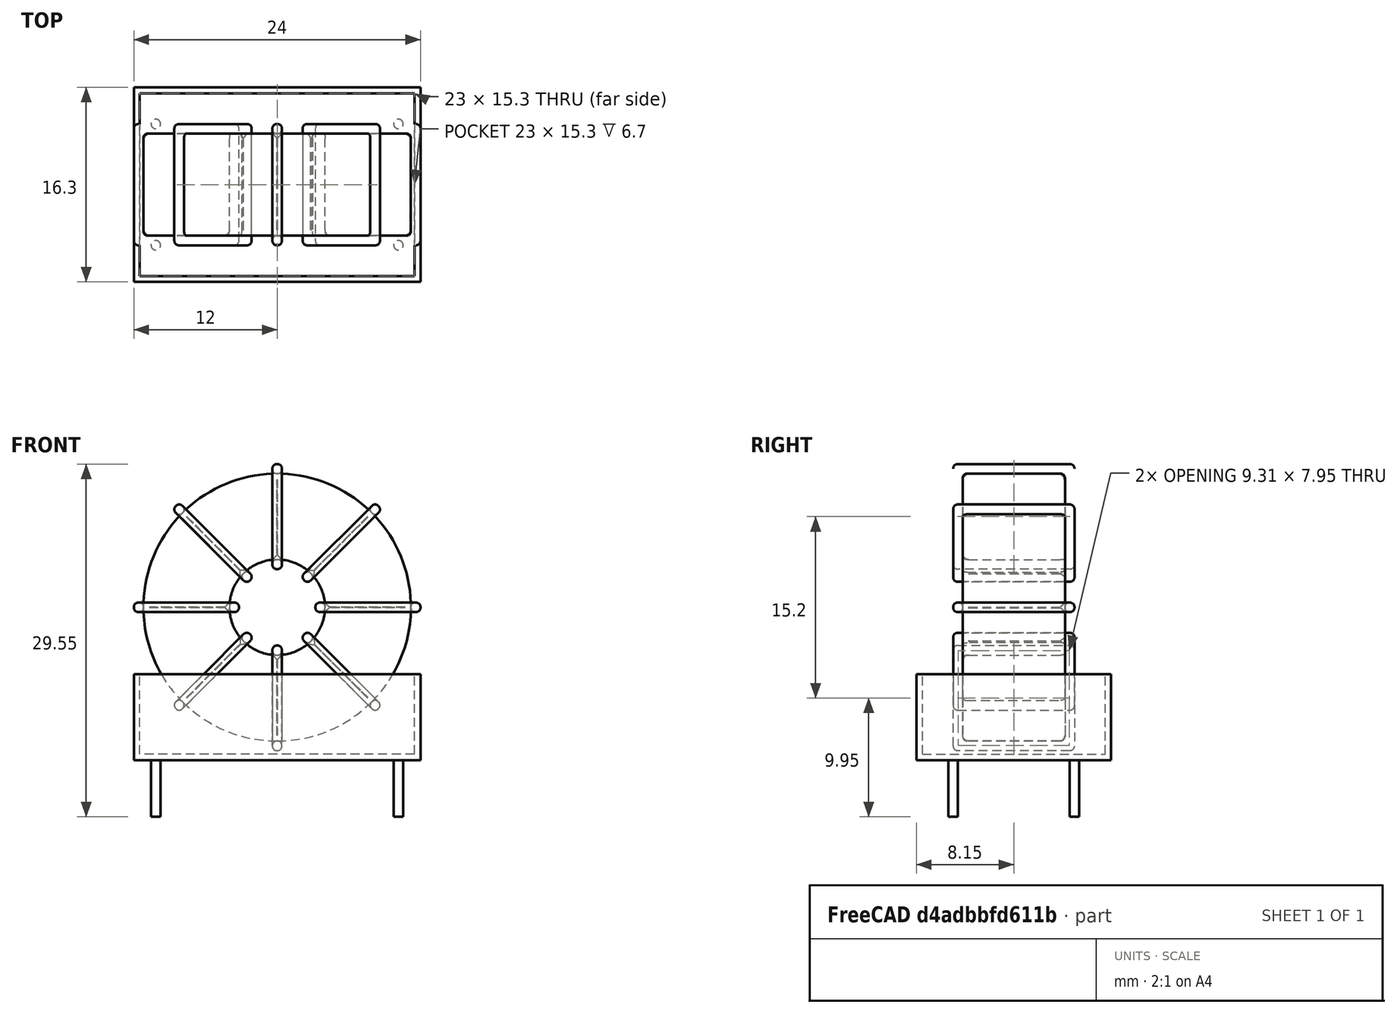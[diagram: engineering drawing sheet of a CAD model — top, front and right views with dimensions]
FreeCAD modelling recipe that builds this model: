
FCSTD DOCUMENT  (FreeCAD 0.16R6712 (Git))
Label: L_CommonMode_Toroid_Vertical_L24.0mm_W16.3mm_Px10.16mm_Py20.32mm_muRATA_5200
License: All rights reserved
LicenseURL: http://en.wikipedia.org/wiki/All_rights_reserved
objects: Sketcher::SketchObject×8, PartDesign::Pad×8, PartDesign::Fillet×5, Spreadsheet::Sheet×1, Part::MultiFuse×1
note: 30 computed .brp shape members not serialized (recipe doc carries the construction recipe); baked Part::Feature solids carry a one-line shape summary decoded from their .brp

FEATURE [Spreadsheet::Sheet] Spreadsheet  label="dimensions"
  cells = A1=Wx; B1(Wx)=24; C1(WW)=8; D1(iWx)=24; A2=Wy; B2(Wy)=10.16; D2(iWy)=16.3; A3=RM; B3(RMx)=10.16; C3(RMy)=20.32; A4=d_wire; B4(d_wire)=0.8; A5=H; B5(H)=31; A6=offsetx; B6(offsetx)=1.84
FEATURE [Sketcher::SketchObject] Sketch
  Placement = pos=(10.16,-5.08,0) rot=(1,0,0;1.5708rad)
  expr: Placement.Base.x = Spreadsheet.RMy / 2
  expr: Constraints[4] = Spreadsheet.WW / 2
  expr: Placement.Base.y = -Spreadsheet.RMx / 2
  expr: Constraints[0] = Spreadsheet.Wx / 2 - Spreadsheet.d_wire
  expr: Constraints[2] = Spreadsheet.Wx / 2 + Spreadsheet.d_wire + 0.5
  sketch-geometry (2):
    g0: Circle CenterX=0 CenterY=13.3 CenterZ=0 NormalX=0 NormalY=0 NormalZ=1 Radius=11.2
    g1: Circle CenterX=0 CenterY=13.3 CenterZ=0 NormalX=0 NormalY=0 NormalZ=1 Radius=4
  constraints (5):
    c: Radius(g0) = 11.2
    c: DistanceX(g-1,g0) = 0
    c: DistanceY(g-1,g0) = 13.3
    c: Coincident(g1,g0)
    c: Radius(g1) = 4
FEATURE [PartDesign::Pad] Pad
  Length = 8.56
  Length2 = 100
  Midplane = true
  Placement = pos=(10.16,-5.08,0) rot=(1,0,0;1.5708rad)
  Sketch = -> Sketch
  Type = 0
  expr: Length = Spreadsheet.Wy - 2 * Spreadsheet.d_wire
FEATURE [Sketcher::SketchObject] Sketch001
  Placement = pos=(0,0,0.75) rot=(0,0,1;0rad)
  expr: Constraints[4] = Spreadsheet.RMy
  expr: Constraints[2] = -Spreadsheet.RMx
  expr: Constraints[1] = Spreadsheet.d_wire / 2
  sketch-geometry (4):
    g0: Circle CenterX=0 CenterY=0 CenterZ=0 NormalX=0 NormalY=0 NormalZ=1 Radius=0.4
    g1: Circle CenterX=20.32 CenterY=-10.16 CenterZ=0 NormalX=0 NormalY=0 NormalZ=1 Radius=0.4
    g2: Circle CenterX=0 CenterY=-10.16 CenterZ=0 NormalX=0 NormalY=0 NormalZ=1 Radius=0.4
    g3: Circle CenterX=20.32 CenterY=0 CenterZ=0 NormalX=0 NormalY=0 NormalZ=1 Radius=0.4
  constraints (11):
    c: Equal(g0,g1)
    c: Radius(g0) = 0.4
    c: DistanceY(g-1,g1) = -10.16
    c: Coincident(g0,g-1)
    c: DistanceX(g-1,g1) = 20.32
    c: PointOnObject(g2,g-2)
    c: DistanceY(g-1,g3) = 0
    c: DistanceY(g2,g1) = 0
    c: DistanceX(g3,g1) = 0
    c: Equal(g3,g2)
    c: Equal(g2,g1)
FEATURE [PartDesign::Pad] Pad001
  Length = 5
  Length2 = 0
  Placement = pos=(0,0,0.75) rot=(0,0,1;0rad)
  Reversed = true
  Sketch = -> Sketch001
  Type = 0
FEATURE [PartDesign::Fillet] Fillet
  Base = -> Pad [Edge6,Edge3,Edge2]
  Placement = pos=(10.16,-5.08,0) rot=(1,0,0;1.5708rad)
  Radius = 0.5
FEATURE [Sketcher::SketchObject] Sketch003
  Placement = pos=(10.16,0,13.3) rot=(1,0,0;3.14159rad)
  expr: Placement.Base.x = Spreadsheet.RMy / 2
  expr: Constraints[18] = Spreadsheet.d_wire
  expr: Constraints[16] = Spreadsheet.d_wire
  expr: Constraints[19] = Spreadsheet.d_wire
  expr: Constraints[17] = Spreadsheet.d_wire
  expr: Placement.Base.y = -1 * (Spreadsheet.RMx - Spreadsheet.Wy) / 2
  expr: Constraints[21] = (Spreadsheet.Wx - Spreadsheet.WW) / 2 - Spreadsheet.d_wire
  expr: Constraints[22] = Spreadsheet.Wx / 2 - Spreadsheet.d_wire
  expr: Constraints[43] = Spreadsheet.d_wire
  expr: Constraints[48] = Spreadsheet.Wx - Spreadsheet.d_wire * 2
  expr: Constraints[49] = Spreadsheet.Wy
  expr: Placement.Base.z = Spreadsheet.Wx / 2 + Spreadsheet.d_wire + 0.5
  sketch-geometry (16):
    g0: LineSegment StartX=-3.2 StartY=0 StartZ=0 EndX=-12 EndY=0 EndZ=0
    g1: LineSegment StartX=-12 StartY=0 StartZ=0 EndX=-12 EndY=10.16 EndZ=0
    g2: LineSegment StartX=-12 StartY=10.16 StartZ=0 EndX=-3.2 EndY=10.16 EndZ=0
    g3: LineSegment StartX=-3.2 StartY=10.16 StartZ=0 EndX=-3.2 EndY=0 EndZ=0
    g4: LineSegment StartX=-11.2 StartY=9.36 StartZ=0 EndX=-4 EndY=9.36 EndZ=0
    g5: LineSegment StartX=-4 StartY=9.36 StartZ=0 EndX=-4 EndY=0.8 EndZ=0
    g6: LineSegment StartX=-4 StartY=0.8 StartZ=0 EndX=-11.2 EndY=0.8 EndZ=0
    g7: LineSegment StartX=-11.2 StartY=0.8 StartZ=0 EndX=-11.2 EndY=9.36 EndZ=0
    g8: LineSegment StartX=3.2 StartY=10.16 StartZ=0 EndX=12 EndY=10.16 EndZ=0
    g9: LineSegment StartX=12 StartY=10.16 StartZ=0 EndX=12 EndY=0 EndZ=0
    g10: LineSegment StartX=12 StartY=0 StartZ=0 EndX=3.2 EndY=0 EndZ=0
    g11: LineSegment StartX=3.2 StartY=0 StartZ=0 EndX=3.2 EndY=10.16 EndZ=0
    g12: LineSegment StartX=4 StartY=9.36 StartZ=0 EndX=11.2 EndY=9.36 EndZ=0
    g13: LineSegment StartX=11.2 StartY=9.36 StartZ=0 EndX=11.2 EndY=0.8 EndZ=0
    g14: LineSegment StartX=11.2 StartY=0.8 StartZ=0 EndX=4 EndY=0.8 EndZ=0
    g15: LineSegment StartX=4 StartY=0.8 StartZ=0 EndX=4 EndY=9.36 EndZ=0
  constraints (50):
    c: Horizontal(g0)
    c: Coincident(g1,g0)
    c: Vertical(g1)
    c: Coincident(g2,g1)
    c: Horizontal(g2)
    c: Coincident(g3,g2)
    c: Coincident(g3,g0)
    c: Vertical(g3)
    c: Coincident(g4,g5)
    c: Coincident(g5,g6)
    c: Coincident(g6,g7)
    c: Coincident(g7,g4)
    c: Horizontal(g4)
    c: Horizontal(g6)
    c: Vertical(g5)
    c: Vertical(g7)
    c: DistanceX(g1,g4) = 0.8
    c: DistanceY(g4,g1) = 0.8
    c: DistanceX(g5,g0) = 0.8
    c: DistanceY(g0,g5) = 0.8
    c: DistanceY(g-1,g0) = 0
    c: DistanceX(g6,g6) = 7.2
    c: DistanceX(g6,g-1) = 11.2
    c: Coincident(g8,g9)
    c: Coincident(g9,g10)
    c: Coincident(g10,g11)
    c: Coincident(g11,g8)
    c: Horizontal(g8)
    c: Horizontal(g10)
    c: Vertical(g9)
    c: Vertical(g11)
    c: Coincident(g12,g13)
    c: Coincident(g13,g14)
    c: Coincident(g14,g15)
    c: Coincident(g15,g12)
    c: Horizontal(g12)
    c: Horizontal(g14)
    c: Vertical(g13)
    c: Vertical(g15)
    c: DistanceY(g8,g2) = 0
    c: DistanceY(g10,g0) = 0
    c: DistanceY(g14,g5) = 0
    c: DistanceY(g12,g4) = 0
    c: DistanceX(g8,g12) = 0.8
    c: Equal(g8,g2)
    c: Equal(g12,g4)
    c: Equal(g9,g1)
    c: Equal(g13,g7)
    c: DistanceX(g4,g12) = 22.4
    c: DistanceY(g0,g1) = 10.16
FEATURE [PartDesign::Pad] Pad002
  Length = 0.8
  Length2 = 100
  Midplane = true
  Placement = pos=(10.16,0,13.3) rot=(1,0,0;3.14159rad)
  Sketch = -> Sketch003
  Type = 0
  expr: Length = Spreadsheet.d_wire
FEATURE [PartDesign::Fillet] Fillet001
  Base = -> Pad002 [Edge38,Edge41,Edge42,Edge43,Edge29,Edge32,Edge33,Edge34,Edge25,Edge35,Edge36,Edge13,Edge14,Edge15,Edge16,Edge17,Edge18,Edge19,Edge1,Edge2,Edge3,Edge4,Edge5,Edge6,Edge7,Edge37,Edge39,Edge40,Edge20,Edge23,Edge24,Edge21,Edge22,Edge8,Edge9,Edge10,Edge11,Edge12,Edge26,Edge27,+8 more]
  Placement = pos=(10.16,0,13.3) rot=(1,0,0;3.14159rad)
  Radius = 0.376
  expr: Radius = Spreadsheet.d_wire * 0.47
FEATURE [Sketcher::SketchObject] Sketch004
  Placement = pos=(10.16,0,13.3) rot=(0.92388,0,0.382683;3.14159rad)
  expr: Placement.Base.x = Spreadsheet.RMy / 2
  expr: Constraints[18] = Spreadsheet.d_wire
  expr: Constraints[16] = Spreadsheet.d_wire
  expr: Constraints[19] = Spreadsheet.d_wire
  expr: Constraints[17] = Spreadsheet.d_wire
  expr: Placement.Base.y = -1 * (Spreadsheet.RMx - Spreadsheet.Wy) / 2
  expr: Constraints[21] = (Spreadsheet.Wx - Spreadsheet.WW) / 2 - Spreadsheet.d_wire
  expr: Constraints[22] = Spreadsheet.Wx / 2 - Spreadsheet.d_wire
  expr: Constraints[43] = Spreadsheet.d_wire
  expr: Constraints[48] = Spreadsheet.Wx - 2 * Spreadsheet.d_wire
  expr: Constraints[49] = Spreadsheet.Wy
  expr: Placement.Base.z = Spreadsheet.Wx / 2 + Spreadsheet.d_wire + 0.5
  sketch-geometry (16):
    g0: LineSegment StartX=-3.2 StartY=0 StartZ=0 EndX=-12 EndY=0 EndZ=0
    g1: LineSegment StartX=-12 StartY=0 StartZ=0 EndX=-12 EndY=10.16 EndZ=0
    g2: LineSegment StartX=-12 StartY=10.16 StartZ=0 EndX=-3.2 EndY=10.16 EndZ=0
    g3: LineSegment StartX=-3.2 StartY=10.16 StartZ=0 EndX=-3.2 EndY=0 EndZ=0
    g4: LineSegment StartX=-11.2 StartY=9.36 StartZ=0 EndX=-4 EndY=9.36 EndZ=0
    g5: LineSegment StartX=-4 StartY=9.36 StartZ=0 EndX=-4 EndY=0.8 EndZ=0
    g6: LineSegment StartX=-4 StartY=0.8 StartZ=0 EndX=-11.2 EndY=0.8 EndZ=0
    g7: LineSegment StartX=-11.2 StartY=0.8 StartZ=0 EndX=-11.2 EndY=9.36 EndZ=0
    g8: LineSegment StartX=3.2 StartY=10.16 StartZ=0 EndX=12 EndY=10.16 EndZ=0
    g9: LineSegment StartX=12 StartY=10.16 StartZ=0 EndX=12 EndY=0 EndZ=0
    g10: LineSegment StartX=12 StartY=0 StartZ=0 EndX=3.2 EndY=0 EndZ=0
    g11: LineSegment StartX=3.2 StartY=0 StartZ=0 EndX=3.2 EndY=10.16 EndZ=0
    g12: LineSegment StartX=4 StartY=9.36 StartZ=0 EndX=11.2 EndY=9.36 EndZ=0
    g13: LineSegment StartX=11.2 StartY=9.36 StartZ=0 EndX=11.2 EndY=0.8 EndZ=0
    g14: LineSegment StartX=11.2 StartY=0.8 StartZ=0 EndX=4 EndY=0.8 EndZ=0
    g15: LineSegment StartX=4 StartY=0.8 StartZ=0 EndX=4 EndY=9.36 EndZ=0
  constraints (50):
    c: Horizontal(g0)
    c: Coincident(g1,g0)
    c: Vertical(g1)
    c: Coincident(g2,g1)
    c: Horizontal(g2)
    c: Coincident(g3,g2)
    c: Coincident(g3,g0)
    c: Vertical(g3)
    c: Coincident(g4,g5)
    c: Coincident(g5,g6)
    c: Coincident(g6,g7)
    c: Coincident(g7,g4)
    c: Horizontal(g4)
    c: Horizontal(g6)
    c: Vertical(g5)
    c: Vertical(g7)
    c: DistanceX(g1,g4) = 0.8
    c: DistanceY(g4,g1) = 0.8
    c: DistanceX(g5,g0) = 0.8
    c: DistanceY(g0,g5) = 0.8
    c: DistanceY(g-1,g0) = 0
    c: DistanceX(g6,g6) = 7.2
    c: DistanceX(g6,g-1) = 11.2
    c: Coincident(g8,g9)
    c: Coincident(g9,g10)
    c: Coincident(g10,g11)
    c: Coincident(g11,g8)
    c: Horizontal(g8)
    c: Horizontal(g10)
    c: Vertical(g9)
    c: Vertical(g11)
    c: Coincident(g12,g13)
    c: Coincident(g13,g14)
    c: Coincident(g14,g15)
    c: Coincident(g15,g12)
    c: Horizontal(g12)
    c: Horizontal(g14)
    c: Vertical(g13)
    c: Vertical(g15)
    c: DistanceY(g8,g2) = 0
    c: DistanceY(g10,g0) = 0
    c: DistanceY(g14,g5) = 0
    c: DistanceY(g12,g4) = 0
    c: DistanceX(g8,g12) = 0.8
    c: Equal(g8,g2)
    c: Equal(g12,g4)
    c: Equal(g9,g1)
    c: Equal(g13,g7)
    c: DistanceX(g4,g12) = 22.4
    c: DistanceY(g0,g1) = 10.16
FEATURE [PartDesign::Pad] Pad003
  Length = 0.8
  Length2 = 100
  Midplane = true
  Placement = pos=(10.16,0,13.3) rot=(0.92388,0,0.382683;3.14159rad)
  Sketch = -> Sketch004
  Type = 0
  expr: Length = Spreadsheet.d_wire
FEATURE [PartDesign::Fillet] Fillet002
  Base = -> Pad003 [Edge38,Edge41,Edge42,Edge43,Edge29,Edge32,Edge33,Edge34,Edge25,Edge35,Edge36,Edge13,Edge14,Edge15,Edge16,Edge17,Edge18,Edge19,Edge1,Edge2,Edge3,Edge4,Edge5,Edge6,Edge7,Edge37,Edge39,Edge40,Edge20,Edge23,Edge24,Edge21,Edge22,Edge8,Edge9,Edge10,Edge11,Edge12,Edge26,Edge27,+8 more]
  Placement = pos=(10.16,0,13.3) rot=(0.92388,0,0.382683;3.14159rad)
  Radius = 0.376
  expr: Radius = Spreadsheet.d_wire * 0.47
FEATURE [Sketcher::SketchObject] Sketch005
  Placement = pos=(10.16,0,13.3) rot=(0.92388,0,-0.382683;3.14159rad)
  expr: Placement.Base.x = Spreadsheet.RMy / 2
  expr: Constraints[18] = Spreadsheet.d_wire
  expr: Constraints[16] = Spreadsheet.d_wire
  expr: Constraints[19] = Spreadsheet.d_wire
  expr: Constraints[17] = Spreadsheet.d_wire
  expr: Placement.Base.y = -1 * (Spreadsheet.RMx - Spreadsheet.Wy) / 2
  expr: Constraints[21] = (Spreadsheet.Wx - Spreadsheet.WW) / 2 - Spreadsheet.d_wire
  expr: Constraints[22] = Spreadsheet.Wx / 2 - Spreadsheet.d_wire
  expr: Constraints[43] = Spreadsheet.d_wire
  expr: Constraints[48] = Spreadsheet.Wx - 2 * Spreadsheet.d_wire
  expr: Constraints[49] = Spreadsheet.Wy
  expr: Placement.Base.z = Spreadsheet.Wx / 2 + Spreadsheet.d_wire + 0.5
  sketch-geometry (16):
    g0: LineSegment StartX=-3.2 StartY=0 StartZ=0 EndX=-12 EndY=0 EndZ=0
    g1: LineSegment StartX=-12 StartY=0 StartZ=0 EndX=-12 EndY=10.16 EndZ=0
    g2: LineSegment StartX=-12 StartY=10.16 StartZ=0 EndX=-3.2 EndY=10.16 EndZ=0
    g3: LineSegment StartX=-3.2 StartY=10.16 StartZ=0 EndX=-3.2 EndY=0 EndZ=0
    g4: LineSegment StartX=-11.2 StartY=9.36 StartZ=0 EndX=-4 EndY=9.36 EndZ=0
    g5: LineSegment StartX=-4 StartY=9.36 StartZ=0 EndX=-4 EndY=0.8 EndZ=0
    g6: LineSegment StartX=-4 StartY=0.8 StartZ=0 EndX=-11.2 EndY=0.8 EndZ=0
    g7: LineSegment StartX=-11.2 StartY=0.8 StartZ=0 EndX=-11.2 EndY=9.36 EndZ=0
    g8: LineSegment StartX=3.2 StartY=10.16 StartZ=0 EndX=12 EndY=10.16 EndZ=0
    g9: LineSegment StartX=12 StartY=10.16 StartZ=0 EndX=12 EndY=0 EndZ=0
    g10: LineSegment StartX=12 StartY=0 StartZ=0 EndX=3.2 EndY=0 EndZ=0
    g11: LineSegment StartX=3.2 StartY=0 StartZ=0 EndX=3.2 EndY=10.16 EndZ=0
    g12: LineSegment StartX=4 StartY=9.36 StartZ=0 EndX=11.2 EndY=9.36 EndZ=0
    g13: LineSegment StartX=11.2 StartY=9.36 StartZ=0 EndX=11.2 EndY=0.8 EndZ=0
    g14: LineSegment StartX=11.2 StartY=0.8 StartZ=0 EndX=4 EndY=0.8 EndZ=0
    g15: LineSegment StartX=4 StartY=0.8 StartZ=0 EndX=4 EndY=9.36 EndZ=0
  constraints (50):
    c: Horizontal(g0)
    c: Coincident(g1,g0)
    c: Vertical(g1)
    c: Coincident(g2,g1)
    c: Horizontal(g2)
    c: Coincident(g3,g2)
    c: Coincident(g3,g0)
    c: Vertical(g3)
    c: Coincident(g4,g5)
    c: Coincident(g5,g6)
    c: Coincident(g6,g7)
    c: Coincident(g7,g4)
    c: Horizontal(g4)
    c: Horizontal(g6)
    c: Vertical(g5)
    c: Vertical(g7)
    c: DistanceX(g1,g4) = 0.8
    c: DistanceY(g4,g1) = 0.8
    c: DistanceX(g5,g0) = 0.8
    c: DistanceY(g0,g5) = 0.8
    c: DistanceY(g-1,g0) = 0
    c: DistanceX(g6,g6) = 7.2
    c: DistanceX(g6,g-1) = 11.2
    c: Coincident(g8,g9)
    c: Coincident(g9,g10)
    c: Coincident(g10,g11)
    c: Coincident(g11,g8)
    c: Horizontal(g8)
    c: Horizontal(g10)
    c: Vertical(g9)
    c: Vertical(g11)
    c: Coincident(g12,g13)
    c: Coincident(g13,g14)
    c: Coincident(g14,g15)
    c: Coincident(g15,g12)
    c: Horizontal(g12)
    c: Horizontal(g14)
    c: Vertical(g13)
    c: Vertical(g15)
    c: DistanceY(g8,g2) = 0
    c: DistanceY(g10,g0) = 0
    c: DistanceY(g14,g5) = 0
    c: DistanceY(g12,g4) = 0
    c: DistanceX(g8,g12) = 0.8
    c: Equal(g8,g2)
    c: Equal(g12,g4)
    c: Equal(g9,g1)
    c: Equal(g13,g7)
    c: DistanceX(g4,g12) = 22.4
    c: DistanceY(g0,g1) = 10.16
FEATURE [PartDesign::Pad] Pad004
  Length = 0.8
  Length2 = 100
  Midplane = true
  Placement = pos=(10.16,0,13.3) rot=(0.92388,0,-0.382683;3.14159rad)
  Sketch = -> Sketch005
  Type = 0
  expr: Length = Spreadsheet.d_wire
FEATURE [PartDesign::Fillet] Fillet003
  Base = -> Pad004 [Edge38,Edge41,Edge42,Edge43,Edge29,Edge32,Edge33,Edge34,Edge25,Edge35,Edge36,Edge13,Edge14,Edge15,Edge16,Edge17,Edge18,Edge19,Edge1,Edge2,Edge3,Edge4,Edge5,Edge6,Edge7,Edge37,Edge39,Edge40,Edge20,Edge23,Edge24,Edge21,Edge22,Edge8,Edge9,Edge10,Edge11,Edge12,Edge26,Edge27,+8 more]
  Placement = pos=(10.16,0,13.3) rot=(0.92388,0,-0.382683;3.14159rad)
  Radius = 0.376
  expr: Radius = Spreadsheet.d_wire * 0.47
FEATURE [Sketcher::SketchObject] Sketch006
  Placement = pos=(10.16,0,13.3) rot=(0.707107,0,0.707107;3.14159rad)
  expr: Placement.Base.x = Spreadsheet.RMy / 2
  expr: Constraints[18] = Spreadsheet.d_wire
  expr: Constraints[16] = Spreadsheet.d_wire
  expr: Constraints[19] = Spreadsheet.d_wire
  expr: Constraints[17] = Spreadsheet.d_wire
  expr: Placement.Base.y = -1 * (Spreadsheet.RMx - Spreadsheet.Wy) / 2
  expr: Constraints[21] = (Spreadsheet.Wx - Spreadsheet.WW) / 2 - Spreadsheet.d_wire
  expr: Constraints[22] = Spreadsheet.Wx / 2 - Spreadsheet.d_wire
  expr: Constraints[43] = Spreadsheet.d_wire
  expr: Constraints[48] = Spreadsheet.Wx - Spreadsheet.d_wire * 2
  expr: Constraints[49] = Spreadsheet.Wy
  expr: Placement.Base.z = Spreadsheet.Wx / 2 + Spreadsheet.d_wire + 0.5
  sketch-geometry (16):
    g0: LineSegment StartX=-3.2 StartY=0 StartZ=0 EndX=-12 EndY=0 EndZ=0
    g1: LineSegment StartX=-12 StartY=0 StartZ=0 EndX=-12 EndY=10.16 EndZ=0
    g2: LineSegment StartX=-12 StartY=10.16 StartZ=0 EndX=-3.2 EndY=10.16 EndZ=0
    g3: LineSegment StartX=-3.2 StartY=10.16 StartZ=0 EndX=-3.2 EndY=0 EndZ=0
    g4: LineSegment StartX=-11.2 StartY=9.36 StartZ=0 EndX=-4 EndY=9.36 EndZ=0
    g5: LineSegment StartX=-4 StartY=9.36 StartZ=0 EndX=-4 EndY=0.8 EndZ=0
    g6: LineSegment StartX=-4 StartY=0.8 StartZ=0 EndX=-11.2 EndY=0.8 EndZ=0
    g7: LineSegment StartX=-11.2 StartY=0.8 StartZ=0 EndX=-11.2 EndY=9.36 EndZ=0
    g8: LineSegment StartX=3.2 StartY=10.16 StartZ=0 EndX=12 EndY=10.16 EndZ=0
    g9: LineSegment StartX=12 StartY=10.16 StartZ=0 EndX=12 EndY=0 EndZ=0
    g10: LineSegment StartX=12 StartY=0 StartZ=0 EndX=3.2 EndY=0 EndZ=0
    g11: LineSegment StartX=3.2 StartY=0 StartZ=0 EndX=3.2 EndY=10.16 EndZ=0
    g12: LineSegment StartX=4 StartY=9.36 StartZ=0 EndX=11.2 EndY=9.36 EndZ=0
    g13: LineSegment StartX=11.2 StartY=9.36 StartZ=0 EndX=11.2 EndY=0.8 EndZ=0
    g14: LineSegment StartX=11.2 StartY=0.8 StartZ=0 EndX=4 EndY=0.8 EndZ=0
    g15: LineSegment StartX=4 StartY=0.8 StartZ=0 EndX=4 EndY=9.36 EndZ=0
  constraints (50):
    c: Horizontal(g0)
    c: Coincident(g1,g0)
    c: Vertical(g1)
    c: Coincident(g2,g1)
    c: Horizontal(g2)
    c: Coincident(g3,g2)
    c: Coincident(g3,g0)
    c: Vertical(g3)
    c: Coincident(g4,g5)
    c: Coincident(g5,g6)
    c: Coincident(g6,g7)
    c: Coincident(g7,g4)
    c: Horizontal(g4)
    c: Horizontal(g6)
    c: Vertical(g5)
    c: Vertical(g7)
    c: DistanceX(g1,g4) = 0.8
    c: DistanceY(g4,g1) = 0.8
    c: DistanceX(g5,g0) = 0.8
    c: DistanceY(g0,g5) = 0.8
    c: DistanceY(g-1,g0) = 0
    c: DistanceX(g6,g6) = 7.2
    c: DistanceX(g6,g-1) = 11.2
    c: Coincident(g8,g9)
    c: Coincident(g9,g10)
    c: Coincident(g10,g11)
    c: Coincident(g11,g8)
    c: Horizontal(g8)
    c: Horizontal(g10)
    c: Vertical(g9)
    c: Vertical(g11)
    c: Coincident(g12,g13)
    c: Coincident(g13,g14)
    c: Coincident(g14,g15)
    c: Coincident(g15,g12)
    c: Horizontal(g12)
    c: Horizontal(g14)
    c: Vertical(g13)
    c: Vertical(g15)
    c: DistanceY(g8,g2) = 0
    c: DistanceY(g10,g0) = 0
    c: DistanceY(g14,g5) = 0
    c: DistanceY(g12,g4) = 0
    c: DistanceX(g8,g12) = 0.8
    c: Equal(g8,g2)
    c: Equal(g12,g4)
    c: Equal(g9,g1)
    c: Equal(g13,g7)
    c: DistanceX(g4,g12) = 22.4
    c: DistanceY(g0,g1) = 10.16
FEATURE [PartDesign::Pad] Pad005
  Length = 0.8
  Length2 = 100
  Midplane = true
  Placement = pos=(10.16,0,13.3) rot=(0.707107,0,0.707107;3.14159rad)
  Sketch = -> Sketch006
  Type = 0
  expr: Length = Spreadsheet.d_wire
FEATURE [PartDesign::Fillet] Fillet004
  Base = -> Pad005 [Edge38,Edge41,Edge42,Edge43,Edge29,Edge32,Edge33,Edge34,Edge25,Edge35,Edge36,Edge13,Edge14,Edge15,Edge16,Edge17,Edge18,Edge19,Edge1,Edge2,Edge3,Edge4,Edge5,Edge6,Edge7,Edge37,Edge39,Edge40,Edge20,Edge23,Edge24,Edge21,Edge22,Edge8,Edge9,Edge10,Edge11,Edge12,Edge26,Edge27,+8 more]
  Placement = pos=(10.16,0,13.3) rot=(0.707107,0,0.707107;3.14159rad)
  Radius = 0.376
  expr: Radius = Spreadsheet.d_wire * 0.47
FEATURE [Sketcher::SketchObject] Sketch007
  Placement = pos=(10.16,0,0.5) rot=(0,0,1;0rad)
  expr: Placement.Base.x = Spreadsheet.RMy / 2
  expr: Placement.Base.z = 0.5
  expr: Constraints[11] = Spreadsheet.iWx / 2
  expr: Constraints[10] = (Spreadsheet.iWy - Spreadsheet.RMx) / 2
  expr: Constraints[9] = Spreadsheet.iWy
  expr: Constraints[8] = Spreadsheet.iWx
  sketch-geometry (4):
    g0: LineSegment StartX=-12 StartY=3.07 StartZ=0 EndX=12 EndY=3.07 EndZ=0
    g1: LineSegment StartX=12 StartY=3.07 StartZ=0 EndX=12 EndY=-13.23 EndZ=0
    g2: LineSegment StartX=12 StartY=-13.23 StartZ=0 EndX=-12 EndY=-13.23 EndZ=0
    g3: LineSegment StartX=-12 StartY=-13.23 StartZ=0 EndX=-12 EndY=3.07 EndZ=0
  constraints (12):
    c: Coincident(g0,g1)
    c: Coincident(g1,g2)
    c: Coincident(g2,g3)
    c: Coincident(g3,g0)
    c: Horizontal(g0)
    c: Horizontal(g2)
    c: Vertical(g1)
    c: Vertical(g3)
    c: DistanceX(g0,g0) = 24
    c: DistanceY(g3,g3) = 16.3
    c: DistanceY(g-1,g0) = 3.07
    c: DistanceX(g0,g-1) = 12
FEATURE [PartDesign::Pad] Pad006
  Length = 0.5
  Length2 = 100
  Placement = pos=(10.16,0,0.5) rot=(0,0,1;0rad)
  Sketch = -> Sketch007
  Type = 0
FEATURE [Sketcher::SketchObject] Sketch008
  Placement = pos=(10.16,0,0.5) rot=(0,0,1;0rad)
  expr: Placement.Base.x = Spreadsheet.RMy / 2
  expr: Constraints[8] = Spreadsheet.iWx
  expr: Constraints[9] = Spreadsheet.iWy
  expr: Constraints[10] = (Spreadsheet.iWy - Spreadsheet.RMx) / 2
  expr: Placement.Base.z = 0.5
  expr: Constraints[21] = 0.5
  expr: Constraints[11] = Spreadsheet.iWx / 2
  sketch-geometry (8):
    g0: LineSegment StartX=-12 StartY=3.07 StartZ=0 EndX=12 EndY=3.07 EndZ=0
    g1: LineSegment StartX=12 StartY=3.07 StartZ=0 EndX=12 EndY=-13.23 EndZ=0
    g2: LineSegment StartX=12 StartY=-13.23 StartZ=0 EndX=-12 EndY=-13.23 EndZ=0
    g3: LineSegment StartX=-12 StartY=-13.23 StartZ=0 EndX=-12 EndY=3.07 EndZ=0
    g4: LineSegment StartX=-11.5 StartY=2.57 StartZ=0 EndX=11.5 EndY=2.57 EndZ=0
    g5: LineSegment StartX=11.5 StartY=2.57 StartZ=0 EndX=11.5 EndY=-12.73 EndZ=0
    g6: LineSegment StartX=11.5 StartY=-12.73 StartZ=0 EndX=-11.5 EndY=-12.73 EndZ=0
    g7: LineSegment StartX=-11.5 StartY=-12.73 StartZ=0 EndX=-11.5 EndY=2.57 EndZ=0
  constraints (24):
    c: Coincident(g0,g1)
    c: Coincident(g1,g2)
    c: Coincident(g2,g3)
    c: Coincident(g3,g0)
    c: Horizontal(g0)
    c: Horizontal(g2)
    c: Vertical(g1)
    c: Vertical(g3)
    c: DistanceX(g0,g0) = 24
    c: DistanceY(g3,g3) = 16.3
    c: DistanceY(g-1,g0) = 3.07
    c: DistanceX(g0,g-1) = 12
    c: Coincident(g4,g5)
    c: Coincident(g5,g6)
    c: Coincident(g6,g7)
    c: Coincident(g7,g4)
    c: Horizontal(g4)
    c: Horizontal(g6)
    c: Vertical(g5)
    c: Vertical(g7)
    c: DistanceX(g5,g1) = 0.5
    c: DistanceY(g1,g5) = 0.5
    c: DistanceX(g0,g4) = 0.5
    c: DistanceY(g4,g0) = 0.5
FEATURE [PartDesign::Pad] Pad007
  Length = 7.2
  Length2 = 100
  Placement = pos=(10.16,0,0.5) rot=(0,0,1;0rad)
  Sketch = -> Sketch008
  Type = 0
  expr: Length = Spreadsheet.Wx * 0.3
FEATURE [Part::MultiFuse] Pad001_mp_cp  label="L_CommonMode_Toroid_Vertical_L24.0mm_W16.3mm_Px10.16mm_Py20.32mm_muRATA_5200"
  Shapes = -> [Pad001,Fillet,Fillet001,Fillet002,Fillet003,Fillet004,Pad006,Pad007]
